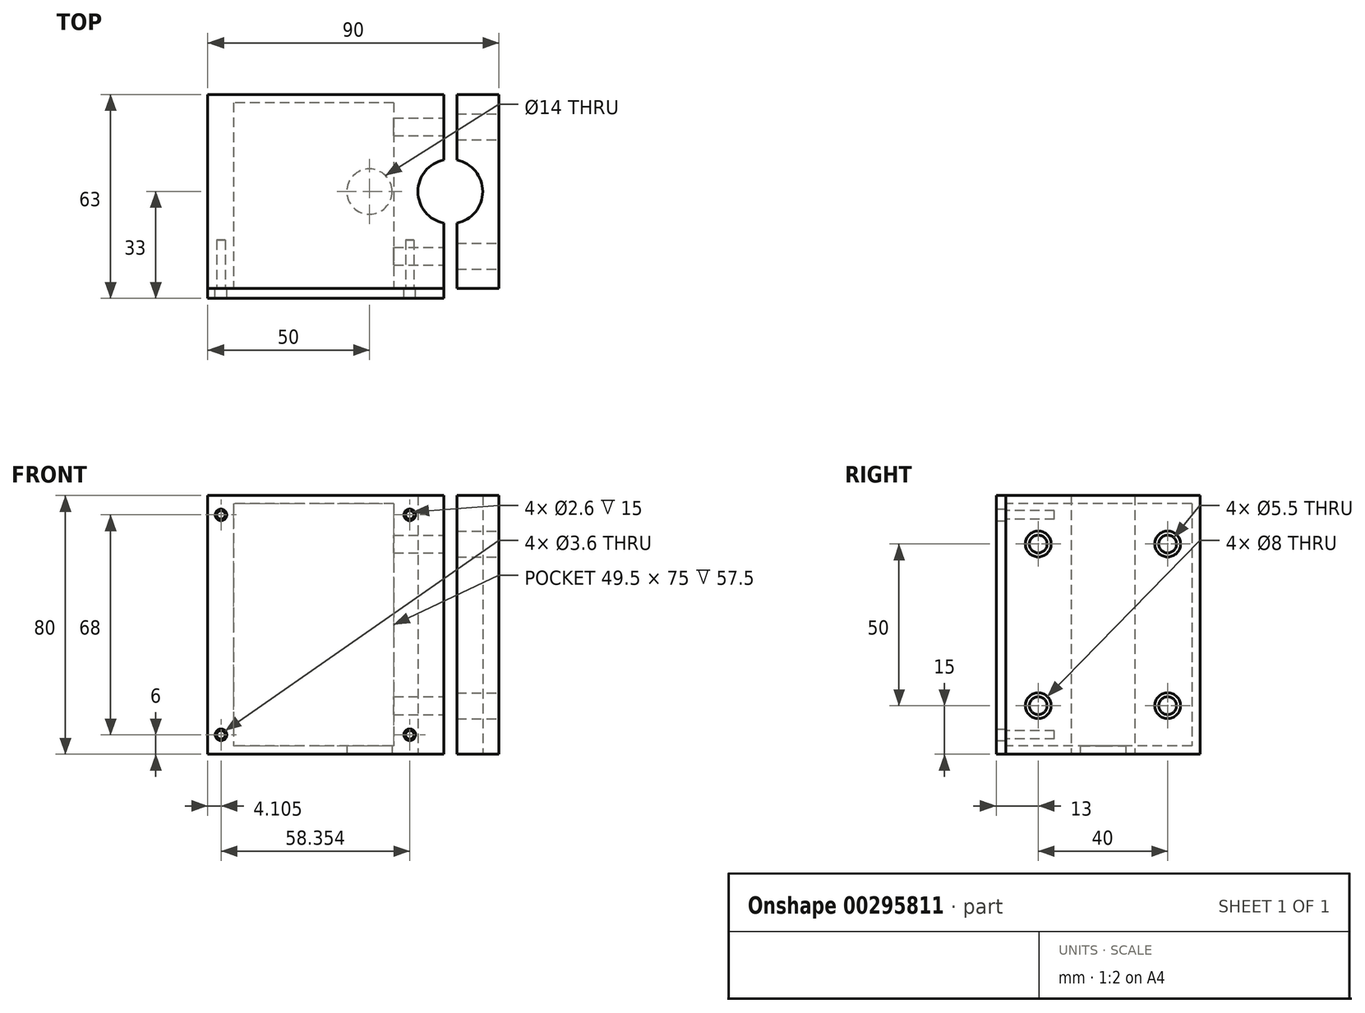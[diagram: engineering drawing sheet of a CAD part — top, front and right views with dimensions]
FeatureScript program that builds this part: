
annotation { "Feature Type Name" : "Feature", "Feature Type Description" : "" }
export const myFeature = defineFeature(function(context is Context, id is Id, definition is map)
    precondition{}
    {
        {
            var Q0;
            Q0=qCreatedBy(makeId("Top.planeOp"),FACE);
            var sketch = newSketch(context, id + "F0", { "sketchPlane" : qUnion([Q0])});
            skCircle(sketch, "E0", {"center": v(15, 0) * mm, "radius": 10 * mm});
            skLineSegment(sketch, "E1.bottom", {"start": v(0, 30) * mm, "end": v(13, 30) * mm});
            skLineSegment(sketch, "E1.top", {"start": v(0, -30) * mm, "end": v(13, -30) * mm});
            skLineSegment(sketch, "E1.left", {"start": v(0, 30) * mm, "end": v(0, -30) * mm});
            skLineSegment(sketch, "E1.right", {"start": v(13, 30) * mm, "end": v(13, -30) * mm});
            skLineSegment(sketch, "E2.bottom", {"start": v(17, 30) * mm, "end": v(30, 30) * mm});
            skLineSegment(sketch, "E2.top", {"start": v(17, -30) * mm, "end": v(30, -30) * mm});
            skLineSegment(sketch, "E2.left", {"start": v(17, 30) * mm, "end": v(17, -30) * mm});
            skLineSegment(sketch, "E2.right", {"start": v(30, 30) * mm, "end": v(30, -30) * mm});
            skLineSegment(sketch, "E3.bottom", {"start": v(0, 30) * mm, "end": v(-60, 30) * mm});
            skLineSegment(sketch, "E3.top", {"start": v(0, -30) * mm, "end": v(-60, -30) * mm});
            skLineSegment(sketch, "E3.right", {"start": v(-60, 30) * mm, "end": v(-60, -30) * mm});
            skSolve(sketch);
        }
        {
            var Q0;
            {var subQ1=sQuery(id+"F0.wireOp",EDGE,"E2.bottom");Q0=makeQuery(id+"F0.imprint","IMPRINT",FACE,{"disambiguationData":[TD([[makeQuery(id+"F0.imprint","IMPRINT",EDGE,{"derivedFrom":subQ1}),-1.0]])]});}
            var Q1;
            {var subQ1=sQuery(id+"F0.wireOp",EDGE,"E1.bottom");Q1=makeQuery(id+"F0.imprint","IMPRINT",FACE,{"disambiguationData":[TD([[makeQuery(id+"F0.imprint","IMPRINT",EDGE,{"derivedFrom":subQ1}),-1.0]])]});}
            extrude(context, id + "F1", {"entities" : qUnion([Q0, Q1]), "depth" : 80 * mm});
        }
        {
            var Q0;
            Q0=makeQuery(id+"F0.imprint","IMPRINT",FACE,{"disambiguationData":[TD([[makeQuery(id+"F0.imprint","IMPRINT",EDGE,{"derivedFrom":sQuery(id+"F0.wireOp",EDGE,"E3.bottom")}),1.0]])]});
            extrude(context, id + "F2", {"entities" : qUnion([Q0]), "depth" : 80 * mm});
        }
        {
            var Q0;
            Q0=makeQuery(id+"F2.opExtrude","SWEPT_FACE",FACE,{"disambiguationData":[OSD([sQuery(id+"F0.wireOp",EDGE,"E3.top")])]});
            shell(context, id + "F3", {"entities" : qUnion([Q0]), "thickness" : 2.5 * mm});
        }
        {
            var Q0;
            Q0=makeQuery(id+"F2.opExtrude","SWEPT_FACE",FACE,{"disambiguationData":[OSD([sQuery(id+"F0.wireOp",EDGE,"E3.right")])]});
            var sketch = newSketch(context, id + "F4", { "sketchPlane" : qUnion([Q0])});
            skLineSegment(sketch, "E4.bottom", {"start": v(-30, 80) * mm, "end": v(30, 80) * mm});
            skLineSegment(sketch, "E4.top", {"start": v(-30, 0) * mm, "end": v(30, 0) * mm});
            skLineSegment(sketch, "E4.left", {"start": v(-30, 80) * mm, "end": v(-30, 0) * mm});
            skLineSegment(sketch, "E4.right", {"start": v(30, 80) * mm, "end": v(30, 0) * mm});
            skSolve(sketch);
        }
        {
            var Q0;
            Q0=makeQuery(id+"F4.imprint","IMPRINT",FACE,{"disambiguationData":[TD([[makeQuery(id+"F4.imprint","IMPRINT",EDGE,{"derivedFrom":sQuery(id+"F4.wireOp",EDGE,"E4.bottom")}),-1.0]])]});
            extrude(context, id + "F5", {"entities" : qUnion([Q0]), "operationType" : NewBodyOperationType.ADD, "oppositeDirection" : true, "depth" : 8 * mm});
        }
        {
            var Q0;
            Q0=makeQuery(id+"F2.opExtrude","SWEPT_BODY",BODY,{"disambiguationData":[OSD([sQuery(id+"F0.wireOp",EDGE,"E3.bottom"),sQuery(id+"F0.wireOp",EDGE,"E3.top"),sQuery(id+"F0.wireOp",EDGE,"E1.left"),sQuery(id+"F0.wireOp",EDGE,"E3.right")])]});
            var Q1;
            Q1=makeQuery(id+"F1.opExtrude","SWEPT_BODY",BODY,{"disambiguationData":[OSD([sQuery(id+"F0.wireOp",EDGE,"E0"),sQuery(id+"F0.wireOp",EDGE,"E1.bottom"),sQuery(id+"F0.wireOp",EDGE,"E1.top"),sQuery(id+"F0.wireOp",EDGE,"E1.right"),sQuery(id+"F0.wireOp",EDGE,"E1.left")])]});
            booleanBodies(context, id + "F6", {"operationType" : BooleanOperationType.UNION, "tools" : qUnion([Q0, Q1])});
        }
        {
            var Q0;
            Q0=makeQuery(id+"F1.opExtrude","SWEPT_FACE",FACE,{"disambiguationData":[OSD([sQuery(id+"F0.wireOp",EDGE,"E2.right")])]});
            var sketch = newSketch(context, id + "F7", { "sketchPlane" : qUnion([Q0])});
            skCircle(sketch, "E5", {"center": v(-20, 65) * mm, "radius": 2.75 * mm});
            skCircle(sketch, "E6", {"center": v(-20, 65) * mm, "radius": 4 * mm});
            skCircle(sketch, "E7", {"center": v(-20, 15) * mm, "radius": 4 * mm});
            skCircle(sketch, "E8", {"center": v(-20, 15) * mm, "radius": 2.75 * mm});
            skCircle(sketch, "E9", {"center": v(20, 65) * mm, "radius": 2.75 * mm});
            skCircle(sketch, "E10", {"center": v(20, 65) * mm, "radius": 4 * mm});
            skCircle(sketch, "E11", {"center": v(20, 15) * mm, "radius": 2.75 * mm});
            skCircle(sketch, "E12", {"center": v(20, 15) * mm, "radius": 4 * mm});
            skSolve(sketch);
        }
        {
            var Q0;
            Q0=makeQuery(id+"F7.imprint","IMPRINT",FACE,{"disambiguationData":[TD([[makeQuery(id+"F7.imprint","IMPRINT",EDGE,{"derivedFrom":sQuery(id+"F7.wireOp",EDGE,"E5")}),1.0]])]});
            var Q1;
            Q1=makeQuery(id+"F7.imprint","IMPRINT",FACE,{"disambiguationData":[TD([[makeQuery(id+"F7.imprint","IMPRINT",EDGE,{"derivedFrom":sQuery(id+"F7.wireOp",EDGE,"E9")}),1.0]])]});
            var Q2;
            Q2=makeQuery(id+"F7.imprint","IMPRINT",FACE,{"disambiguationData":[TD([[makeQuery(id+"F7.imprint","IMPRINT",EDGE,{"derivedFrom":sQuery(id+"F7.wireOp",EDGE,"E11")}),1.0]])]});
            var Q3;
            Q3=makeQuery(id+"F7.imprint","IMPRINT",FACE,{"disambiguationData":[TD([[makeQuery(id+"F7.imprint","IMPRINT",EDGE,{"derivedFrom":sQuery(id+"F7.wireOp",EDGE,"E8")}),1.0]])]});
            extrude(context, id + "F8", {"entities" : qUnion([Q0, Q1, Q2, Q3]), "operationType" : NewBodyOperationType.REMOVE, "oppositeDirection" : true, "depth" : 35 * mm});
        }
        {
            var Q0;
            Q0=makeQuery(id+"F7.imprint","IMPRINT",FACE,{"disambiguationData":[TD([[makeQuery(id+"F7.imprint","IMPRINT",EDGE,{"derivedFrom":sQuery(id+"F7.wireOp",EDGE,"E5")}),-1.0]])]});
            var Q1;
            Q1=makeQuery(id+"F7.imprint","IMPRINT",FACE,{"disambiguationData":[TD([[makeQuery(id+"F7.imprint","IMPRINT",EDGE,{"derivedFrom":sQuery(id+"F7.wireOp",EDGE,"E9")}),-1.0]])]});
            var Q2;
            Q2=makeQuery(id+"F7.imprint","IMPRINT",FACE,{"disambiguationData":[TD([[makeQuery(id+"F7.imprint","IMPRINT",EDGE,{"derivedFrom":sQuery(id+"F7.wireOp",EDGE,"E11")}),-1.0]])]});
            var Q3;
            Q3=makeQuery(id+"F7.imprint","IMPRINT",FACE,{"disambiguationData":[TD([[makeQuery(id+"F7.imprint","IMPRINT",EDGE,{"derivedFrom":sQuery(id+"F7.wireOp",EDGE,"E7")}),1.0]])]});
            extrude(context, id + "F9", {"entities" : qUnion([Q0, Q1, Q2, Q3]), "operationType" : NewBodyOperationType.REMOVE, "oppositeDirection" : true, "depth" : 15 * mm});
        }
        {
            var Q0;
            Q0=makeQuery(id+"F0.imprint","IMPRINT",FACE,{"disambiguationData":[TD([[makeQuery(id+"F0.imprint","IMPRINT",EDGE,{"derivedFrom":sQuery(id+"F0.wireOp",EDGE,"E3.bottom")}),1.0]])]});
            var sketch = newSketch(context, id + "F10", { "sketchPlane" : qUnion([Q0])});
            skCircle(sketch, "E13", {"center": v(-10, 0) * mm, "radius": 7 * mm});
            skSolve(sketch);
        }
        {
            var Q0;
            Q0=makeQuery(id+"F10.imprint","IMPRINT",FACE,{"disambiguationData":[TD([[makeQuery(id+"F10.imprint","IMPRINT",EDGE,{"derivedFrom":sQuery(id+"F10.wireOp",EDGE,"E13")}),1.0]])]});
            extrude(context, id + "F11", {"entities" : qUnion([Q0]), "operationType" : NewBodyOperationType.REMOVE, "depth" : 25 * mm});
        }
        {
            var Q0;
            Q0=makeQuery(id+"F6.opBoolean","MERGE",FACE,{"derivedFrom":[makeQuery(id+"F1.opExtrude","SWEPT_FACE",FACE,{"disambiguationData":[OSD([sQuery(id+"F0.wireOp",EDGE,"E1.top")])]}),makeQuery(id+"F5.boolean.opBoolean","MERGE",FACE,{"derivedFrom":[makeQuery(id+"F2.opExtrude","SWEPT_FACE",FACE,{"disambiguationData":[OSD([sQuery(id+"F0.wireOp",EDGE,"E3.top")])]}),makeQuery(id+"F5.opExtrude","SWEPT_FACE",FACE,{"disambiguationData":[OSD([sQuery(id+"F4.wireOp",EDGE,"E4.right")])]})]})]});
            var sketch = newSketch(context, id + "F12", { "sketchPlane" : qUnion([Q0])});
            skLineSegment(sketch, "E14.bottom", {"start": v(13, 80) * mm, "end": v(-60, 80) * mm});
            skLineSegment(sketch, "E14.top", {"start": v(13, 0) * mm, "end": v(-60, 0) * mm});
            skLineSegment(sketch, "E14.left", {"start": v(13, 80) * mm, "end": v(13, 0) * mm});
            skLineSegment(sketch, "E14.right", {"start": v(-60, 80) * mm, "end": v(-60, 0) * mm});
            skCircle(sketch, "E15", {"center": v(-55.9, 74) * mm, "radius": 1.8 * mm});
            skCircle(sketch, "E16", {"center": v(-55.9, 6) * mm, "radius": 1.8 * mm});
            skCircle(sketch, "E17", {"center": v(2.46, 74) * mm, "radius": 1.8 * mm});
            skCircle(sketch, "E18", {"center": v(2.46, 6) * mm, "radius": 1.8 * mm});
            skCircle(sketch, "E19", {"center": v(-55.9, 74) * mm, "radius": 1.3 * mm});
            skCircle(sketch, "E20", {"center": v(-55.9, 6) * mm, "radius": 1.3 * mm});
            skCircle(sketch, "E21", {"center": v(2.46, 74) * mm, "radius": 1.3 * mm});
            skCircle(sketch, "E22", {"center": v(2.46, 6) * mm, "radius": 1.3 * mm});
            skSolve(sketch);
        }
        {
            var Q0;
            Q0=makeQuery(id+"F12.imprint","IMPRINT",FACE,{"disambiguationData":[TD([[makeQuery(id+"F12.imprint","IMPRINT",EDGE,{"derivedFrom":sQuery(id+"F12.wireOp",EDGE,"E14.bottom")}),1.0]])]});
            var Q1;
            Q1=makeQuery(id+"F12.imprint","IMPRINT",FACE,{"disambiguationData":[TD([[makeQuery(id+"F12.imprint","IMPRINT",EDGE,{"derivedFrom":makeQuery(id+"F5.opExtrude","CAP_EDGE",EDGE,{"disambiguationData":[OSD([sQuery(id+"F4.wireOp",EDGE,"E4.right")])],"isStart":false})}),1.0]])]});
            extrude(context, id + "F13", {"entities" : qUnion([Q0, Q1]), "depth" : 3 * mm});
        }
        {
            var Q0;
            Q0=makeQuery(id+"F12.imprint","IMPRINT",FACE,{"disambiguationData":[TD([[makeQuery(id+"F12.imprint","IMPRINT",EDGE,{"derivedFrom":sQuery(id+"F12.wireOp",EDGE,"E19")}),1.0]])]});
            var Q1;
            Q1=makeQuery(id+"F12.imprint","IMPRINT",FACE,{"disambiguationData":[TD([[makeQuery(id+"F12.imprint","IMPRINT",EDGE,{"derivedFrom":sQuery(id+"F12.wireOp",EDGE,"E21")}),1.0]])]});
            var Q2;
            Q2=makeQuery(id+"F12.imprint","IMPRINT",FACE,{"disambiguationData":[TD([[makeQuery(id+"F12.imprint","IMPRINT",EDGE,{"derivedFrom":sQuery(id+"F12.wireOp",EDGE,"E20")}),1.0]])]});
            var Q3;
            Q3=makeQuery(id+"F12.imprint","IMPRINT",FACE,{"disambiguationData":[TD([[makeQuery(id+"F12.imprint","IMPRINT",EDGE,{"derivedFrom":sQuery(id+"F12.wireOp",EDGE,"E22")}),1.0]])]});
            extrude(context, id + "F14", {"entities" : qUnion([Q0, Q1, Q2, Q3]), "operationType" : NewBodyOperationType.REMOVE, "oppositeDirection" : true, "depth" : 15 * mm});
        }
    });
